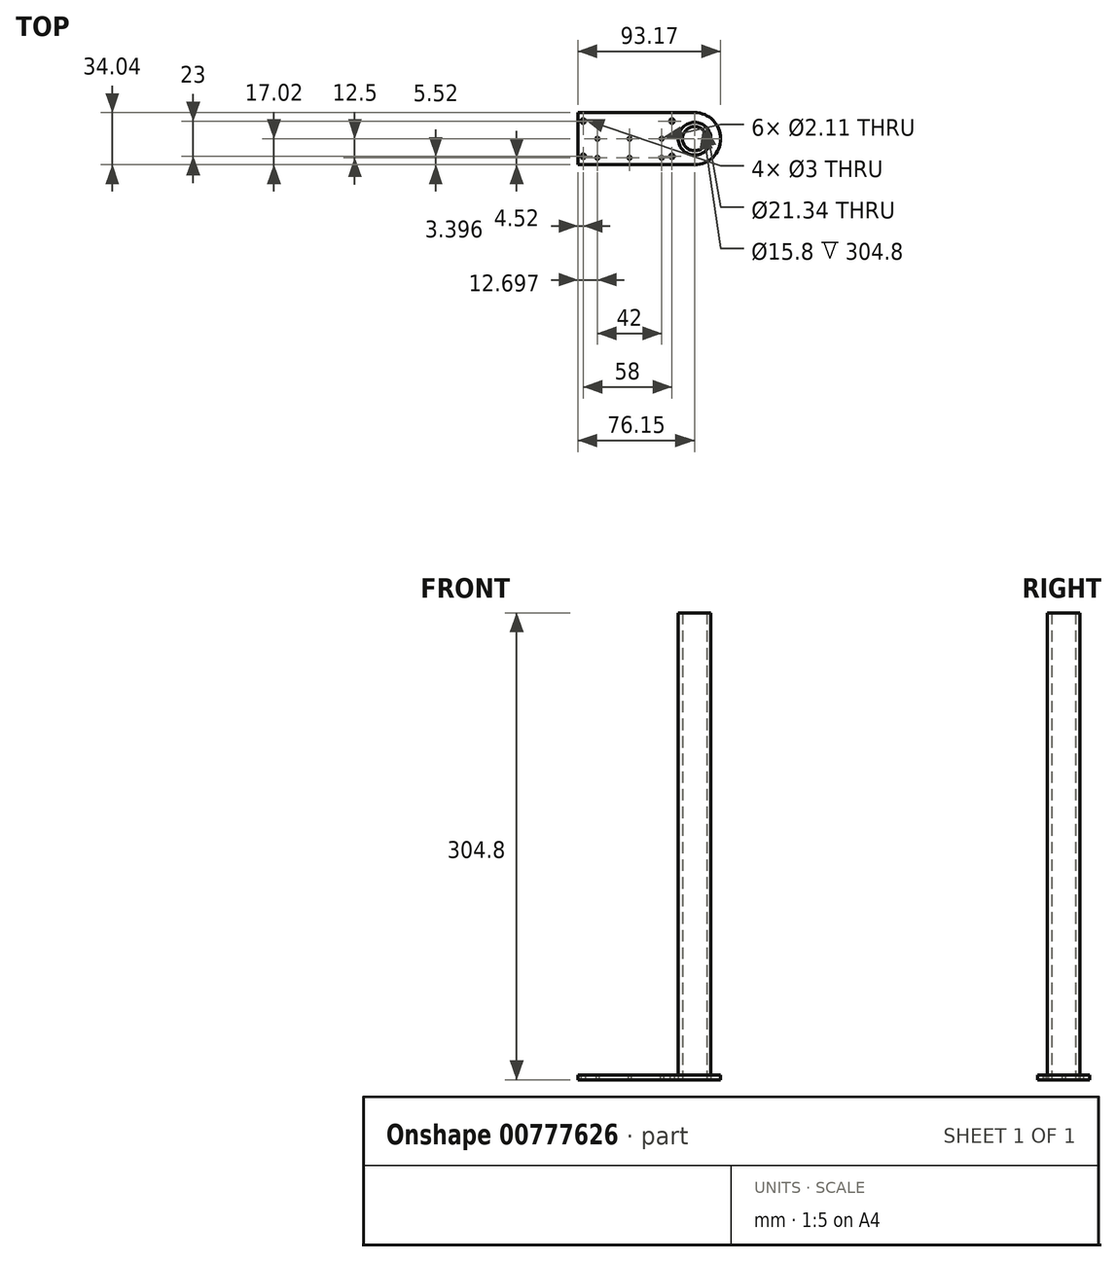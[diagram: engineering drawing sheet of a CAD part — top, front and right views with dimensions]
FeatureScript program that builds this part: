
annotation { "Feature Type Name" : "Feature", "Feature Type Description" : "" }
export const myFeature = defineFeature(function(context is Context, id is Id, definition is map)
    precondition{}
    {
        {
            var Q0;
            Q0=qCreatedBy(makeId("Top.planeOp"),FACE);
            var sketch = newSketch(context, id + "F0", { "sketchPlane" : qUnion([Q0])});
            skCircle(sketch, "E0", {"center": v(0, 0) * mm, "radius": 10.67 * mm});
            skCircle(sketch, "E1", {"center": v(0, 0) * mm, "radius": 7.9 * mm});
            skSolve(sketch);
        }
        {
            var Q0;
            Q0=makeQuery(id+"F0.imprint","IMPRINT",FACE,{"disambiguationData":[TD([[makeQuery(id+"F0.imprint","IMPRINT",EDGE,{"derivedFrom":sQuery(id+"F0.wireOp",EDGE,"E0")}),1.0]])]});
            extrude(context, id + "F1", {"entities" : qUnion([Q0]), "depth" : 304.8 * mm, "offsetDistance" : 25.4 * mm});
        }
        {
            var Q0;
            Q0=makeQuery(id+"F1.opExtrude","CAP_FACE",FACE,{"disambiguationData":[OSD([sQuery(id+"F0.wireOp",EDGE,"E0"),sQuery(id+"F0.wireOp",EDGE,"E1")])],"isStart":true});
            var sketch = newSketch(context, id + "F2", { "sketchPlane" : qUnion([Q0])});
            skArc(sketch, "E2.0", {"start": v(0, -17.02) * mm, "mid": v(17.02, 0) * mm, "end": v(0, 17.02) * mm});
            skLineSegment(sketch, "E3.bottom", {"start": v(0, 17.02) * mm, "end": v(-76.15, 17.02) * mm});
            skLineSegment(sketch, "E3.top", {"start": v(0, -17.02) * mm, "end": v(-76.15, -17.02) * mm});
            skLineSegment(sketch, "E3.right", {"start": v(-76.15, 17.02) * mm, "end": v(-76.15, -17.02) * mm});
            skSolve(sketch);
        }
        {
            var Q0;
            Q0=makeQuery(id+"F2.imprint","IMPRINT",FACE,{"disambiguationData":[TD([[makeQuery(id+"F2.imprint","IMPRINT",EDGE,{"derivedFrom":sQuery(id+"F2.wireOp",EDGE,"E2.0")}),1.0]])]});
            extrude(context, id + "F3", {"entities" : qUnion([Q0]), "oppositeDirection" : true, "depth" : 3.17 * mm, "offsetDistance" : 25.4 * mm});
        }
        {
            var Q0;
            Q0=makeQuery(id+"F3.opExtrude","CAP_FACE",FACE,{"disambiguationData":[OSD([sQuery(id+"F0.wireOp",EDGE,"E0"),sQuery(id+"F2.wireOp",EDGE,"E2.0"),sQuery(id+"F2.wireOp",EDGE,"E3.bottom"),sQuery(id+"F2.wireOp",EDGE,"E3.top"),sQuery(id+"F2.wireOp",EDGE,"E3.right")])],"isStart":true});
            var sketch = newSketch(context, id + "F4", { "sketchPlane" : qUnion([Q0])});
            skLineSegment(sketch, "E4", {"start": v(-83.28, 24.72) * mm, "end": v(-33.72, 24.72) * mm, "construction": true});
            skCircle(sketch, "E5", {"center": v(-63.45, 0) * mm, "radius": 1.06 * mm});
            skCircle(sketch, "E6.0.1.0", {"center": v(-63.45, 12.5) * mm, "radius": 1.06 * mm});
            skCircle(sketch, "E6.1.0.0", {"center": v(-42.45, 0) * mm, "radius": 1.06 * mm});
            skCircle(sketch, "E6.1.1.0", {"center": v(-42.45, 12.5) * mm, "radius": 1.06 * mm});
            skCircle(sketch, "E6.2.0.0", {"center": v(-21.45, 0) * mm, "radius": 1.06 * mm});
            skCircle(sketch, "E6.2.1.0", {"center": v(-21.45, 12.5) * mm, "radius": 1.06 * mm});
            skLineSegment(sketch, "E6.direction1", {"start": v(-63.45, 0) * mm, "end": v(-42.45, 0) * mm, "construction": true});
            skLineSegment(sketch, "E6.direction2", {"start": v(-63.45, 12.5) * mm, "end": v(-63.45, 0) * mm, "construction": true});
            skSolve(sketch);
        }
        {
            var Q0;
            Q0 = qSketchRegion(id + "F4", true);
            extrude(context, id + "F5", {"entities" : qUnion([Q0]), "operationType" : NewBodyOperationType.REMOVE, "endBound" : BoundingType.UP_TO_NEXT, "oppositeDirection" : true, "depth" : 25.4 * mm, "offsetDistance" : 25.4 * mm});
        }
        {
            var Q0;
            Q0=makeQuery(id+"F3.opExtrude","CAP_FACE",FACE,{"disambiguationData":[OSD([sQuery(id+"F0.wireOp",EDGE,"E0"),sQuery(id+"F2.wireOp",EDGE,"E2.0"),sQuery(id+"F2.wireOp",EDGE,"E3.bottom"),sQuery(id+"F2.wireOp",EDGE,"E3.top"),sQuery(id+"F2.wireOp",EDGE,"E3.right")])],"isStart":true});
            var sketch = newSketch(context, id + "F6", { "sketchPlane" : qUnion([Q0])});
            skCircle(sketch, "E7", {"center": v(-72.75, 11.5) * mm, "radius": 1.5 * mm});
            skCircle(sketch, "E8.0.1.0", {"center": v(-72.75, -11.5) * mm, "radius": 1.5 * mm});
            skCircle(sketch, "E8.1.0.0", {"center": v(-14.75, 11.5) * mm, "radius": 1.5 * mm});
            skCircle(sketch, "E8.1.1.0", {"center": v(-14.75, -11.5) * mm, "radius": 1.5 * mm});
            skLineSegment(sketch, "E8.direction1", {"start": v(-72.75, 11.5) * mm, "end": v(-14.75, 11.5) * mm, "construction": true});
            skLineSegment(sketch, "E8.direction2", {"start": v(-72.75, 11.5) * mm, "end": v(-72.75, -11.5) * mm, "construction": true});
            skSolve(sketch);
        }
        {
            var Q0;
            Q0 = qSketchRegion(id + "F6", true);
            extrude(context, id + "F7", {"entities" : qUnion([Q0]), "operationType" : NewBodyOperationType.REMOVE, "endBound" : BoundingType.UP_TO_NEXT, "oppositeDirection" : true, "depth" : 25.4 * mm, "offsetDistance" : 25.4 * mm});
        }
    });
